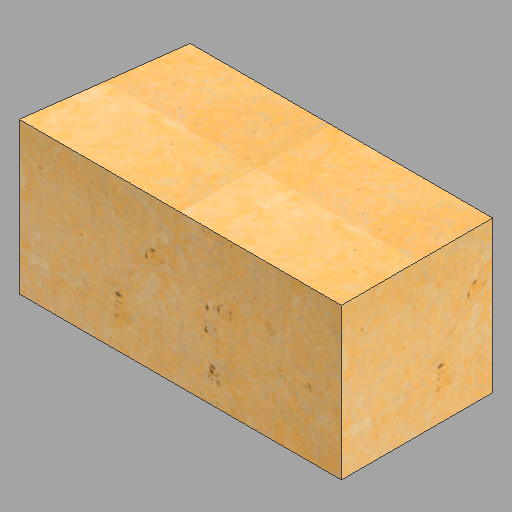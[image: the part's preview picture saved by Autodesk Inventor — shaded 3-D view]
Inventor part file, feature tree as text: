
AUTODESK INVENTOR PART (.ipt)
format: ipt  version: 2023 (Build 270158000, 158)  size: 385,536 bytes
history: native  units: in
note: dims shown in document units (in); Inventor stores cm internally (conversion verified against a paired STEP export)
features: other x1, extrude x1, sketch x1
ambient origin geometry x8: Origin, YZ Plane, XZ Plane, XY Plane, X Axis, Y Axis, Z Axis, Center Point
bodies: Solid1 (feature_tree)
feature tree (3):
  other  "B - 2"
  extrude  "Extrusion1"  Depth=24.0in
  sketch  "Sketch1"  dims[d0=48.0in d1=24.0in d2=51.125in d3=24.0in d4=0.0in]
